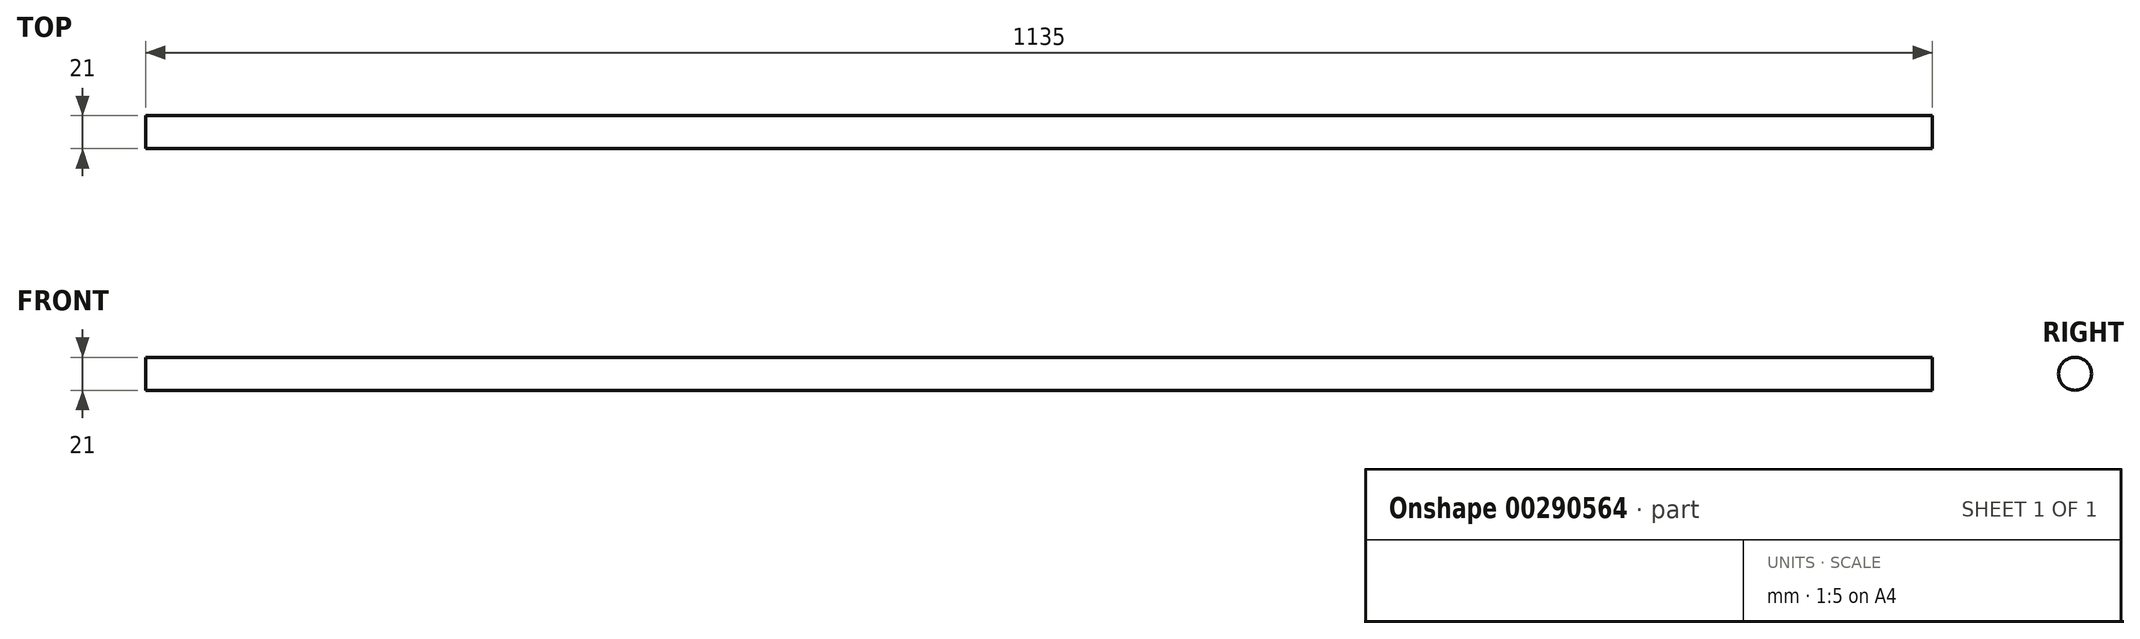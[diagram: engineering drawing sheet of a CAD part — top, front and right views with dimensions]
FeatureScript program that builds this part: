
annotation { "Feature Type Name" : "Feature", "Feature Type Description" : "" }
export const myFeature = defineFeature(function(context is Context, id is Id, definition is map)
    precondition{}
    {
        {
            var Q0;
            Q0=qCreatedBy(makeId("Right.planeOp"),FACE);
            var sketch = newSketch(context, id + "F0", { "sketchPlane" : qUnion([Q0])});
            skCircle(sketch, "E0", {"center": v(0, 0) * mm, "radius": 10.5 * mm});
            skSolve(sketch);
        }
        {
            var Q0;
            Q0=makeQuery(id+"F0.imprint","IMPRINT",FACE,{"disambiguationData":[TD([[makeQuery(id+"F0.imprint","IMPRINT",EDGE,{"derivedFrom":sQuery(id+"F0.wireOp",EDGE,"E0")}),1.0]])]});
            extrude(context, id + "F1", {"entities" : qUnion([Q0]), "depth" : 1135 * mm});
        }
    });
